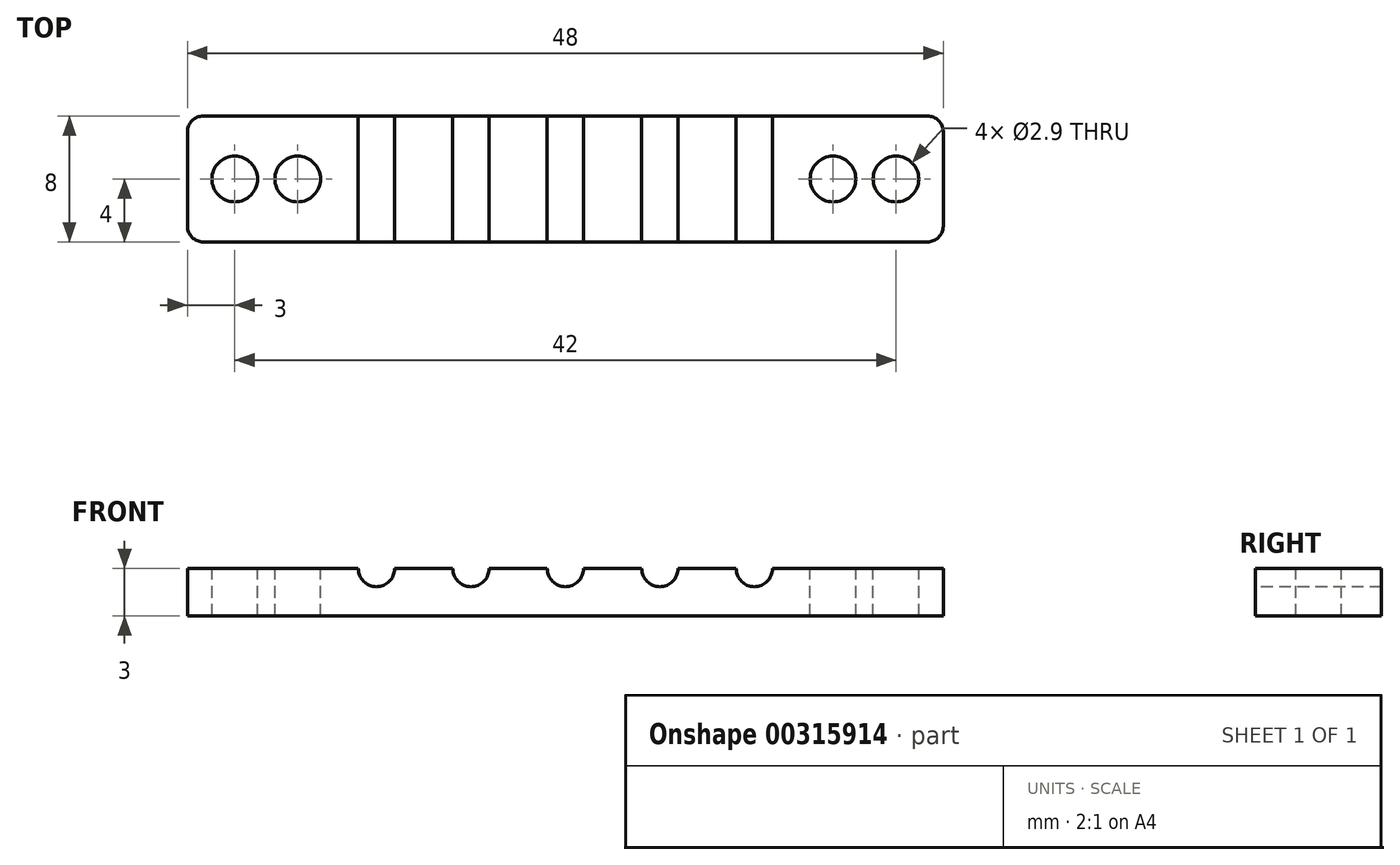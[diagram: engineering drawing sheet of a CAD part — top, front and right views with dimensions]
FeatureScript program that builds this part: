
annotation { "Feature Type Name" : "Feature", "Feature Type Description" : "" }
export const myFeature = defineFeature(function(context is Context, id is Id, definition is map)
    precondition{}
    {
        {
            var Q0;
            Q0=qCreatedBy(makeId("Top.planeOp"),FACE);
            var sketch = newSketch(context, id + "F0", { "sketchPlane" : qUnion([Q0])});
            skLineSegment(sketch, "E0.bottom", {"start": v(3, 4) * mm, "end": v(-3, 4) * mm});
            skLineSegment(sketch, "E0.top", {"start": v(3, -4) * mm, "end": v(-3, -4) * mm});
            skLineSegment(sketch, "E0.left", {"start": v(3, 4) * mm, "end": v(3, -4) * mm});
            skLineSegment(sketch, "E0.right", {"start": v(-3, 4) * mm, "end": v(-3, -4) * mm});
            skPoint(sketch, "E0.middle", {"position": v(0, 0) * mm});
            skLineSegment(sketch, "E1.bottom", {"start": v(45, 4) * mm, "end": v(39, 4) * mm});
            skLineSegment(sketch, "E1.top", {"start": v(45, -4) * mm, "end": v(39, -4) * mm});
            skLineSegment(sketch, "E1.left", {"start": v(45, 4) * mm, "end": v(45, -4) * mm});
            skLineSegment(sketch, "E1.right", {"start": v(39, 4) * mm, "end": v(39, -4) * mm});
            skPoint(sketch, "E1.middle", {"position": v(42, 0) * mm});
            skLineSegment(sketch, "E2", {"start": v(3, 4) * mm, "end": v(39, 4) * mm});
            skLineSegment(sketch, "E3", {"start": v(3, -4) * mm, "end": v(39, -4) * mm});
            skLineSegment(sketch, "E4", {"start": v(9, 4) * mm, "end": v(9, -4) * mm, "construction": true});
            skLineSegment(sketch, "E5.direction1", {"start": v(9, -4) * mm, "end": v(15, -4) * mm, "construction": true});
            skPoint(sketch, "E6", {"position": v(4, 0) * mm});
            skPoint(sketch, "E6.positionSnap0", {"position": v(3, 0) * mm});
            skPoint(sketch, "E7", {"position": v(38, 0) * mm});
            skPoint(sketch, "E7.positionSnap0", {"position": v(39, 0) * mm});
            skLineSegment(sketch, "E8.0.1.0", {"start": v(15, 4) * mm, "end": v(15, -4) * mm, "construction": true});
            skLineSegment(sketch, "E8.0.2.0", {"start": v(21, 4) * mm, "end": v(21, -4) * mm, "construction": true});
            skLineSegment(sketch, "E8.0.3.0", {"start": v(27, 4) * mm, "end": v(27, -4) * mm, "construction": true});
            skLineSegment(sketch, "E8.0.4.0", {"start": v(33, 4) * mm, "end": v(33, -4) * mm, "construction": true});
            skSolve(sketch);
        }
        {
            var Q0;
            Q0=makeQuery(id+"F0.imprint","IMPRINT",FACE,{"disambiguationData":[TD([[makeQuery(id+"F0.imprint","IMPRINT",EDGE,{"derivedFrom":sQuery(id+"F0.wireOp",EDGE,"E0.bottom")}),1.0]])]});
            var Q1;
            Q1=makeQuery(id+"F0.imprint","IMPRINT",FACE,{"disambiguationData":[TD([[makeQuery(id+"F0.imprint","IMPRINT",EDGE,{"derivedFrom":sQuery(id+"F0.wireOp",EDGE,"E0.left")}),1.0]])]});
            var Q2;
            Q2=makeQuery(id+"F0.imprint","IMPRINT",FACE,{"disambiguationData":[TD([[makeQuery(id+"F0.imprint","IMPRINT",EDGE,{"derivedFrom":sQuery(id+"F0.wireOp",EDGE,"E1.bottom")}),1.0]])]});
            extrude(context, id + "F1", {"entities" : qUnion([Q0, Q1, Q2]), "oppositeDirection" : true, "depth" : 3 * mm});
        }
        {
            var Q0;
            Q0=sQuery(id+"F0.wireOp",VERTEX,"E0.middle");
            var Q1;
            Q1=sQuery(id+"F0.wireOp",VERTEX,"E6");
            var Q2;
            Q2=sQuery(id+"F0.wireOp",VERTEX,"E7");
            var Q3;
            Q3=sQuery(id+"F0.wireOp",VERTEX,"E1.middle");
            var Q4;
            Q4=makeQuery(id+"F1.opExtrude","SWEPT_BODY",BODY,{"disambiguationData":[OSD([sQuery(id+"F0.wireOp",EDGE,"E0.bottom"),sQuery(id+"F0.wireOp",EDGE,"E0.top"),sQuery(id+"F0.wireOp",EDGE,"E0.right"),sQuery(id+"F0.wireOp",EDGE,"E1.bottom"),sQuery(id+"F0.wireOp",EDGE,"E1.top"),sQuery(id+"F0.wireOp",EDGE,"E1.left"),sQuery(id+"F0.wireOp",EDGE,"E2"),sQuery(id+"F0.wireOp",EDGE,"E3")])]});
            hole(context, id + "F2", {"style" : HoleStyle.SIMPLE, "endStyle" : HoleEndStyle.THROUGH, "holeDiameter" : 2.9 * mm, "tappedDepth" : 12 * mm, "tapClearance" : 3, "locations" : qUnion([Q0, Q1, Q2, Q3]), "scope" : qUnion([Q4])});
        }
        {
            var Q0;
            {var subQ0=sQuery(id+"F0.wireOp",EDGE,"E3");var subQ1=sQuery(id+"F0.wireOp",EDGE,"E1.top");var subQ2=sQuery(id+"F0.wireOp",EDGE,"E0.top");Q0=makeQuery(id+"FaaVOSY5iOmgxNq_1.boolean.opBoolean","MERGE",FACE,{"derivedFrom":[makeQuery(id+"F1.opExtrude","SWEPT_FACE",FACE,{"disambiguationData":[OSD([subQ2,subQ1,subQ0])]}),makeQuery(id+"FaaVOSY5iOmgxNq_1.opExtrude","SWEPT_FACE",FACE,{"disambiguationData":[OSD([subQ2,subQ1,subQ0])]})]});}
            var sketch = newSketch(context, id + "F3", { "sketchPlane" : qUnion([Q0])});
            skPoint(sketch, "E9", {"position": v(9, 0) * mm});
            skLineSegment(sketch, "E10.direction1", {"start": v(9, 0) * mm, "end": v(15, 0) * mm, "construction": true});
            skPoint(sketch, "E11.0.1.0", {"position": v(15, 0) * mm});
            skPoint(sketch, "E11.0.2.0", {"position": v(21, 0) * mm});
            skPoint(sketch, "E11.0.3.0", {"position": v(27, 0) * mm});
            skPoint(sketch, "E11.0.4.0", {"position": v(33, 0) * mm});
            skSolve(sketch);
        }
        {
            var Q0;
            Q0=sQuery(id+"F3.wireOp",VERTEX,"E9");
            var Q1;
            Q1=sQuery(id+"F3.wireOp",VERTEX,"E11.0.1.0");
            var Q2;
            Q2=sQuery(id+"F3.wireOp",VERTEX,"E11.0.2.0");
            var Q3;
            Q3=sQuery(id+"F3.wireOp",VERTEX,"E11.0.3.0");
            var Q4;
            Q4=sQuery(id+"F3.wireOp",VERTEX,"E11.0.4.0");
            var Q5;
            Q5=makeQuery(id+"F1.opExtrude","SWEPT_BODY",BODY,{"disambiguationData":[OSD([sQuery(id+"F0.wireOp",EDGE,"E0.bottom"),sQuery(id+"F0.wireOp",EDGE,"E0.top"),sQuery(id+"F0.wireOp",EDGE,"E0.right"),sQuery(id+"F0.wireOp",EDGE,"E1.bottom"),sQuery(id+"F0.wireOp",EDGE,"E1.top"),sQuery(id+"F0.wireOp",EDGE,"E1.left"),sQuery(id+"F0.wireOp",EDGE,"E2"),sQuery(id+"F0.wireOp",EDGE,"E3")])]});
            hole(context, id + "F4", {"style" : HoleStyle.SIMPLE, "endStyle" : HoleEndStyle.THROUGH, "holeDiameter" : 2.3 * mm, "tappedDepth" : 12 * mm, "tapClearance" : 3, "locations" : qUnion([Q0, Q1, Q2, Q3, Q4]), "scope" : qUnion([Q5])});
        }
        {
            var Q0;
            Q0=makeQuery(id+"F1.opExtrude","SWEPT_EDGE",EDGE,{"disambiguationData":[OSD([sQuery(id+"F0.wireOp",EDGE,"E0.top"),sQuery(id+"F0.wireOp",EDGE,"E0.right")])]});
            var Q1;
            Q1=makeQuery(id+"F1.opExtrude","SWEPT_EDGE",EDGE,{"disambiguationData":[OSD([sQuery(id+"F0.wireOp",EDGE,"E1.top"),sQuery(id+"F0.wireOp",EDGE,"E1.left")])]});
            var Q2;
            Q2=makeQuery(id+"F1.opExtrude","SWEPT_EDGE",EDGE,{"disambiguationData":[OSD([sQuery(id+"F0.wireOp",EDGE,"E1.bottom"),sQuery(id+"F0.wireOp",EDGE,"E1.left")])]});
            var Q3;
            Q3=makeQuery(id+"F1.opExtrude","SWEPT_EDGE",EDGE,{"disambiguationData":[OSD([sQuery(id+"F0.wireOp",EDGE,"E0.bottom"),sQuery(id+"F0.wireOp",EDGE,"E0.right")])]});
            fillet(context, id + "F5", {"entities" : qUnion([Q0, Q1, Q2, Q3]), "radius" : 1 * mm, "tangentPropagation" : true, "allowEdgeOverflow" : false});
        }
    });
